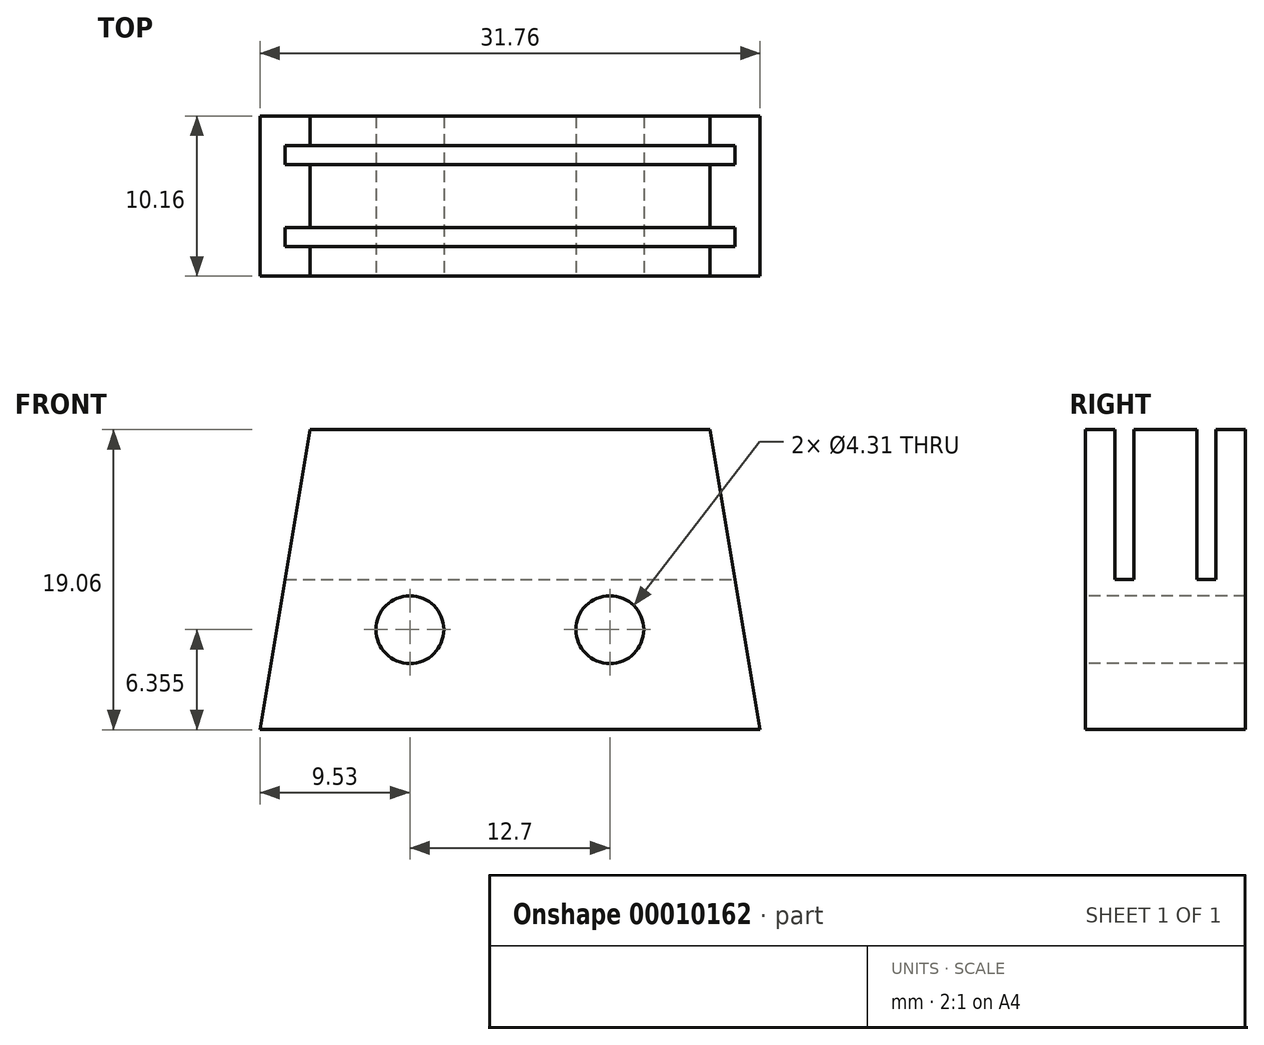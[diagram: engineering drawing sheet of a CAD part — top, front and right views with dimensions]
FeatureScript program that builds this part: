
annotation { "Feature Type Name" : "Feature", "Feature Type Description" : "" }
export const myFeature = defineFeature(function(context is Context, id is Id, definition is map)
    precondition{}
    {
        {
            var Q0;
            Q0=qCreatedBy(makeId("Top.planeOp"),FACE);
            var sketch = newSketch(context, id + "F0", { "sketchPlane" : qUnion([Q0])});
            skLineSegment(sketch, "E0.rect.bottom", {"start": v(15.88, 9.52) * mm, "end": v(-15.88, 9.52) * mm});
            skLineSegment(sketch, "E0.rect.top", {"start": v(15.88, -9.53) * mm, "end": v(-15.88, -9.53) * mm});
            skLineSegment(sketch, "E0.rect.left", {"start": v(15.88, 9.52) * mm, "end": v(15.88, -9.53) * mm});
            skLineSegment(sketch, "E0.rect.right", {"start": v(-15.88, 9.52) * mm, "end": v(-15.88, -9.53) * mm});
            skPoint(sketch, "E0.rect.middle", {"position": v(0, 0) * mm});
            skSolve(sketch);
        }
        {
            var Q0;
            Q0 = qSketchRegion(id + "F0", true);
            extrude(context, id + "F1", {"entities" : qUnion([Q0]), "depth" : 10.16 * mm});
        }
        {
            var Q0;
            Q0=makeQuery(id+"F1.opExtrude","CAP_FACE",FACE,{"disambiguationData":[OSD([sQuery(id+"F0.wireOp",EDGE,"E0.rect.bottom"),sQuery(id+"F0.wireOp",EDGE,"E0.rect.top"),sQuery(id+"F0.wireOp",EDGE,"E0.rect.left"),sQuery(id+"F0.wireOp",EDGE,"E0.rect.right")])],"isStart":false});
            var sketch = newSketch(context, id + "F2", { "sketchPlane" : qUnion([Q0])});
            skCircle(sketch, "E1", {"center": v(-6.35, -3.18) * mm, "radius": 2.15 * mm});
            skCircle(sketch, "E2", {"center": v(6.35, -3.18) * mm, "radius": 2.15 * mm});
            skSolve(sketch);
        }
        {
            var Q0;
            Q0 = qSketchRegion(id + "F2", true);
            extrude(context, id + "F3", {"entities" : qUnion([Q0]), "operationType" : NewBodyOperationType.REMOVE, "endBound" : BoundingType.UP_TO_NEXT, "oppositeDirection" : true, "depth" : 25.4 * mm});
        }
        {
            var Q0;
            Q0=makeQuery(id+"F1.opExtrude","SWEPT_FACE",FACE,{"disambiguationData":[OSD([sQuery(id+"F0.wireOp",EDGE,"E0.rect.bottom")])]});
            var sketch = newSketch(context, id + "F4", { "sketchPlane" : qUnion([Q0])});
            skLineSegment(sketch, "E3.rect.bottom", {"start": v(19.05, 1.88) * mm, "end": v(-19.05, 1.88) * mm});
            skLineSegment(sketch, "E3.rect.top", {"start": v(19.05, 3.08) * mm, "end": v(-19.05, 3.08) * mm});
            skLineSegment(sketch, "E3.rect.left", {"start": v(19.05, 1.88) * mm, "end": v(19.05, 3.08) * mm});
            skLineSegment(sketch, "E3.rect.right", {"start": v(-19.05, 1.88) * mm, "end": v(-19.05, 3.08) * mm});
            skPoint(sketch, "E3.rect.middle", {"position": v(0, 2.48) * mm});
            skLineSegment(sketch, "E4", {"start": v(-15.88, 5.08) * mm, "end": v(15.88, 5.08) * mm, "construction": true});
            skLineSegment(sketch, "E5.rect.bottom", {"start": v(-15.88, 7.08) * mm, "end": v(15.88, 7.08) * mm});
            skLineSegment(sketch, "E5.rect.top", {"start": v(-15.88, 8.28) * mm, "end": v(15.88, 8.28) * mm});
            skLineSegment(sketch, "E5.rect.left", {"start": v(-15.88, 7.08) * mm, "end": v(-15.88, 8.28) * mm});
            skLineSegment(sketch, "E5.rect.right", {"start": v(15.88, 7.08) * mm, "end": v(15.88, 8.28) * mm});
            skPoint(sketch, "E5.rect.middle", {"position": v(0, 7.68) * mm});
            skSolve(sketch);
        }
        {
            var Q0;
            Q0 = qSketchRegion(id + "F4", true);
            extrude(context, id + "F5", {"entities" : qUnion([Q0]), "operationType" : NewBodyOperationType.REMOVE, "oppositeDirection" : true, "depth" : 9.52 * mm});
        }
        {
            var Q0;
            Q0=qCreatedBy(makeId("Front.planeOp"),FACE);
            var sketch = newSketch(context, id + "F6", { "sketchPlane" : qUnion([Q0])});
            skLineSegment(sketch, "E6", {"start": v(77.64, 0) * mm, "end": v(-79.2, 0) * mm, "construction": true});
            skSolve(sketch);
        }
        {
            var Q0;
            Q0=makeQuery(id+"F1.opExtrude","CAP_FACE",FACE,{"disambiguationData":[OSD([sQuery(id+"F0.wireOp",EDGE,"E0.rect.bottom"),sQuery(id+"F0.wireOp",EDGE,"E0.rect.top"),sQuery(id+"F0.wireOp",EDGE,"E0.rect.left"),sQuery(id+"F0.wireOp",EDGE,"E0.rect.right")])],"isStart":false});
            var sketch = newSketch(context, id + "F7", { "sketchPlane" : qUnion([Q0])});
            skLineSegment(sketch, "E7", {"start": v(15.88, -9.53) * mm, "end": v(12.7, 9.53) * mm});
            skLineSegment(sketch, "E8", {"start": v(12.7, 9.52) * mm, "end": v(15.88, 9.52) * mm});
            skLineSegment(sketch, "E9", {"start": v(15.88, 9.52) * mm, "end": v(15.88, -9.53) * mm});
            skLineSegment(sketch, "E10", {"start": v(-15.88, -9.53) * mm, "end": v(-15.88, 9.52) * mm});
            skLineSegment(sketch, "E11", {"start": v(-15.88, 9.52) * mm, "end": v(-12.7, 9.52) * mm});
            skLineSegment(sketch, "E12", {"start": v(-12.7, 9.53) * mm, "end": v(-15.88, -9.53) * mm});
            skSolve(sketch);
        }
        {
            var Q0;
            Q0 = qSketchRegion(id + "F7", true);
            var Q1;
            Q1=makeQuery(id+"F1.opExtrude","CAP_FACE",FACE,{"disambiguationData":[OSD([sQuery(id+"F0.wireOp",EDGE,"E0.rect.bottom"),sQuery(id+"F0.wireOp",EDGE,"E0.rect.top"),sQuery(id+"F0.wireOp",EDGE,"E0.rect.left"),sQuery(id+"F0.wireOp",EDGE,"E0.rect.right")])],"isStart":true});
            extrude(context, id + "F8", {"entities" : qUnion([Q0]), "operationType" : NewBodyOperationType.REMOVE, "endBound" : BoundingType.UP_TO_SURFACE, "oppositeDirection" : true, "endBoundEntityFace" : qUnion([Q1]), "depth" : 25.4 * mm});
        }
        {
            var Q0;
            Q0=makeQuery(id+"F1.opExtrude","SWEPT_BODY",BODY,{"disambiguationData":[OSD([sQuery(id+"F0.wireOp",EDGE,"E0.rect.bottom"),sQuery(id+"F0.wireOp",EDGE,"E0.rect.top"),sQuery(id+"F0.wireOp",EDGE,"E0.rect.left"),sQuery(id+"F0.wireOp",EDGE,"E0.rect.right")])]});
            var Q1;
            Q1=sQuery(id+"F6.wireOp",EDGE,"E6");
            transform(context, id + "F9", {"entities" : qUnion([Q0]), "transformType" : TransformType.ROTATION, "transformAxis" : qUnion([Q1]), "angle" : 90 * degree, "oppositeDirection" : true, "makeCopy" : false});
        }
    });
